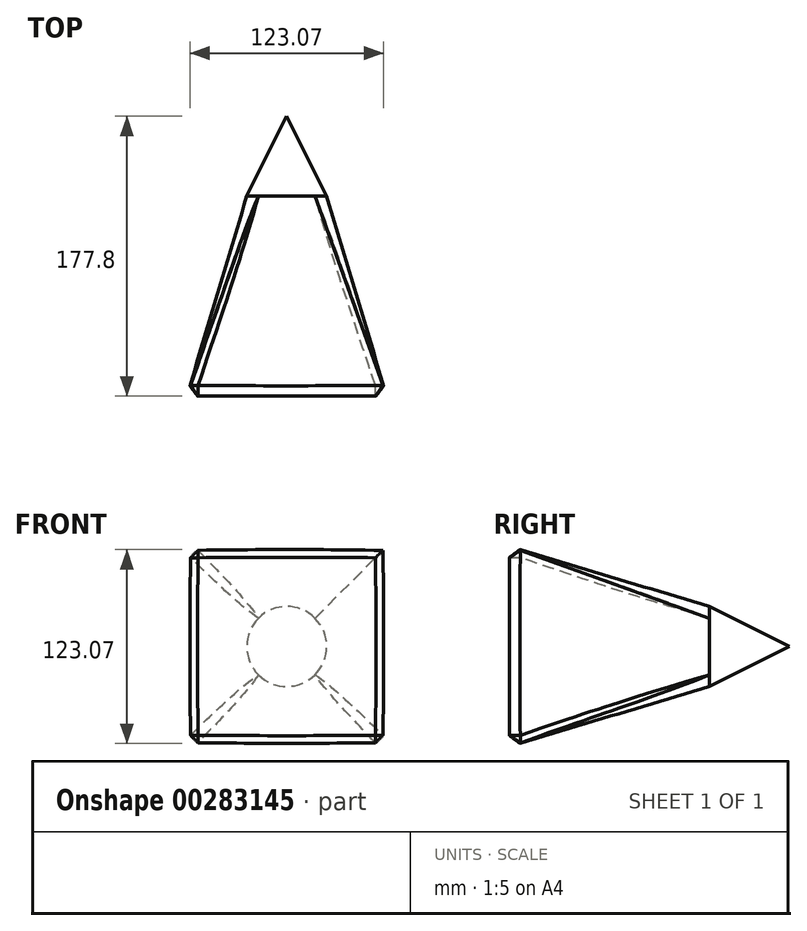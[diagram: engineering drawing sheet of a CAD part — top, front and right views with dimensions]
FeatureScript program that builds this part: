
annotation { "Feature Type Name" : "Feature", "Feature Type Description" : "" }
export const myFeature = defineFeature(function(context is Context, id is Id, definition is map)
    precondition{}
    {
        {
            var Q0;
            Q0=qCreatedBy(makeId("Front.planeOp"),FACE);
            var sketch = newSketch(context, id + "F0", { "sketchPlane" : qUnion([Q0])});
            skCircle(sketch, "E0", {"center": v(0, 0) * mm, "radius": 25.4 * mm});
            skSolve(sketch);
        }
        {
            var Q0;
            Q0=qCreatedBy(makeId("Front.planeOp"),FACE);
            cPlane(context, id + "F1", {"entities" : qUnion([Q0]), "cplaneType" : CPlaneType.OFFSET, "offset" : 127 * mm, "width" : 152.4 * mm, "height" : 152.4 * mm});
        }
        {
            var Q0;
            Q0=qCreatedBy(id+"F1.planeOp",FACE);
            var sketch = newSketch(context, id + "F2", { "sketchPlane" : qUnion([Q0])});
            skLineSegment(sketch, "E1.bottom", {"start": v(63.5, -63.5) * mm, "end": v(-63.5, -63.5) * mm});
            skLineSegment(sketch, "E1.top", {"start": v(63.5, 63.5) * mm, "end": v(-63.5, 63.5) * mm});
            skLineSegment(sketch, "E1.left", {"start": v(63.5, -63.5) * mm, "end": v(63.5, 63.5) * mm});
            skLineSegment(sketch, "E1.right", {"start": v(-63.5, -63.5) * mm, "end": v(-63.5, 63.5) * mm});
            skPoint(sketch, "E1.middle", {"position": v(0, 0) * mm});
            skSolve(sketch);
        }
        {
            var Q0;
            Q0=makeQuery(id+"F0.imprint","IMPRINT",FACE,{"disambiguationData":[TD([[makeQuery(id+"F0.imprint","IMPRINT",EDGE,{"derivedFrom":sQuery(id+"F0.wireOp",EDGE,"E0")}),1.0]])]});
            var Q1;
            Q1=makeQuery(id+"F2.imprint","IMPRINT",FACE,{"disambiguationData":[TD([[makeQuery(id+"F2.imprint","IMPRINT",EDGE,{"derivedFrom":sQuery(id+"F2.wireOp",EDGE,"E1.bottom")}),-1.0]])]});
            loft(context, id + "F3", {"sheetProfilesArray" : [{ "sheetProfileEntities" : qUnion([Q0]) }, { "sheetProfileEntities" : qUnion([Q1]) }]});
        }
        {
            var Q0;
            Q0=qCreatedBy(makeId("Front.planeOp"),FACE);
            cPlane(context, id + "F4", {"entities" : qUnion([Q0]), "cplaneType" : CPlaneType.OFFSET, "offset" : 50.8 * mm, "oppositeDirection" : true, "width" : 152.4 * mm, "height" : 152.4 * mm});
        }
        {
            var Q0;
            Q0=qCreatedBy(id+"F4.planeOp",FACE);
            var sketch = newSketch(context, id + "F5", { "sketchPlane" : qUnion([Q0])});
            skCircle(sketch, "E2", {"center": v(0, 0) * mm, "radius": 0.38 * mm});
            skSolve(sketch);
        }
        {
            var Q1;
            Q1=makeQuery(id+"F3.opLoft","CAP_FACE",FACE,{"disambiguationData":[OSD([makeQuery(id+"F0.imprint","IMPRINT",FACE,{"disambiguationData":[TD([[makeQuery(id+"F0.imprint","IMPRINT",EDGE,{"derivedFrom":sQuery(id+"F0.wireOp",EDGE,"E0")}),1.0]])]})])],"isStart":true});
            var Q2;
            Q2=sQuery(id+"F5.wireOp",VERTEX,"E2.center");
            loft(context, id + "F6", {"operationType" : NewBodyOperationType.ADD, "sheetProfilesArray" : [{ "sheetProfileEntities" : qUnion([Q1]) }, { "sheetProfileEntities" : qUnion([Q2]) }]});
        }
        {
            var Q0;
            Q0=makeQuery(id+"F3.opLoft","MID_CAP_EDGE",EDGE,{"disambiguationData":[OSD([sQuery(id+"F2.wireOp",EDGE,"E1.bottom"),sQuery(id+"F2.wireOp",EDGE,"E1.top"),sQuery(id+"F2.wireOp",EDGE,"E1.right")])],"capPos":1.0});
            var Q1;
            Q1=makeQuery(id+"F3.opLoft","MID_CAP_EDGE",EDGE,{"disambiguationData":[OSD([sQuery(id+"F2.wireOp",EDGE,"E1.bottom"),sQuery(id+"F2.wireOp",EDGE,"E1.left"),sQuery(id+"F2.wireOp",EDGE,"E1.right")])],"capPos":1.0});
            var Q2;
            Q2=makeQuery(id+"F3.opLoft","MID_CAP_EDGE",EDGE,{"disambiguationData":[OSD([sQuery(id+"F2.wireOp",EDGE,"E1.bottom"),sQuery(id+"F2.wireOp",EDGE,"E1.top"),sQuery(id+"F2.wireOp",EDGE,"E1.left")])],"capPos":1.0});
            var Q3;
            Q3=makeQuery(id+"F3.opLoft","MID_CAP_EDGE",EDGE,{"disambiguationData":[OSD([sQuery(id+"F2.wireOp",EDGE,"E1.top"),sQuery(id+"F2.wireOp",EDGE,"E1.left"),sQuery(id+"F2.wireOp",EDGE,"E1.right")])],"capPos":1.0});
            var Q4;
            Q4=makeQuery(id+"F3.opLoft","SWEPT_EDGE",EDGE,{"disambiguationData":[OSD([sQuery(id+"F2.wireOp",EDGE,"E1.bottom"),sQuery(id+"F2.wireOp",EDGE,"E1.left")])]});
            var Q5;
            Q5=makeQuery(id+"F3.opLoft","SWEPT_EDGE",EDGE,{"disambiguationData":[OSD([sQuery(id+"F0.wireOp",EDGE,"E0"),sQuery(id+"F2.wireOp",EDGE,"E1.bottom"),sQuery(id+"F2.wireOp",EDGE,"E1.top"),sQuery(id+"F2.wireOp",EDGE,"E1.right")])]});
            var Q6;
            Q6=makeQuery(id+"F3.opLoft","SWEPT_EDGE",EDGE,{"disambiguationData":[OSD([sQuery(id+"F0.wireOp",EDGE,"E0"),sQuery(id+"F2.wireOp",EDGE,"E1.top"),sQuery(id+"F2.wireOp",EDGE,"E1.left"),sQuery(id+"F2.wireOp",EDGE,"E1.right")])]});
            var Q7;
            Q7=makeQuery(id+"F3.opLoft","SWEPT_EDGE",EDGE,{"disambiguationData":[OSD([sQuery(id+"F0.wireOp",EDGE,"E0"),sQuery(id+"F2.wireOp",EDGE,"E1.bottom"),sQuery(id+"F2.wireOp",EDGE,"E1.top"),sQuery(id+"F2.wireOp",EDGE,"E1.left")])]});
            chamfer(context, id + "F7", {"entities" : qUnion([Q0, Q1, Q2, Q3, Q4, Q5, Q6, Q7]), "width" : 5.08 * mm, "tangentPropagation" : true});
        }
    });
